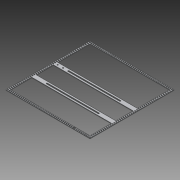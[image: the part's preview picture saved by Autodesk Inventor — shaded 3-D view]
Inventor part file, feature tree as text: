
AUTODESK INVENTOR PART (.ipt)
format: ipt  version: 2014 SP1 (Build 180222100, 222)  size: 398,848 bytes
history: native  units: in
note: dims shown in document units (in); Inventor stores cm internally (conversion verified against a paired STEP export)
features: reference x5, extrude x1, sketch x1
ambient origin geometry x8: Origin, YZ Plane, XZ Plane, XY Plane, X Axis, Y Axis, Z Axis, Center Point
bodies: Solid1 (feature_tree)
feature tree (7):
  extrude  "Extrusion1"  Depth=19.5in
  sketch  "Sketch1"  dims[d0=19.5in d1=19.5in d2=0.5in d3=0.266in d4=0.25in d5=0.25in d6=19.685in d8=0.3878in d9=0.7874in d11=19.0in d14=13.7795in d16=0.4357in d17=0.3937in d19=1.0in d21=1.0in d22=1.0in d23=5.0in d24=10.0in d25=3.5in d26=3.5in d27=3.0in d28=3.0in d33=0.125in d34=0.0in d36=3.5433in d38=0.4688in d39=0.3937in d41=1.0in d43=0.4357in d44=0.4688in d45=0.3in]
  reference  "Reference1"
  reference  "Reference2"
  reference  "Reference3"
  reference  "Reference4"
  reference  "Reference5"
